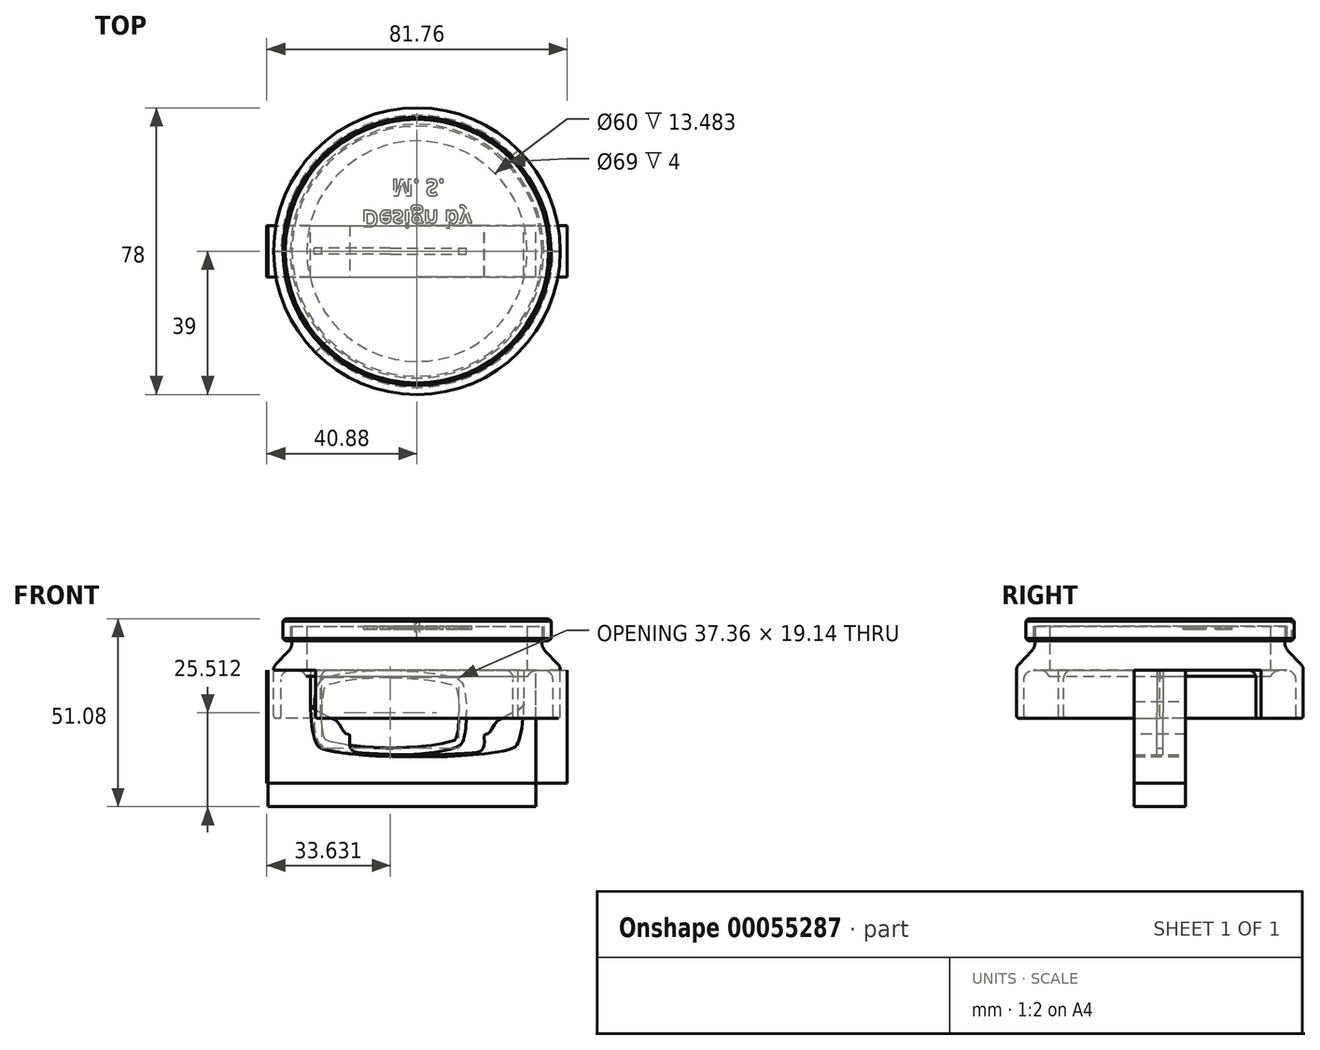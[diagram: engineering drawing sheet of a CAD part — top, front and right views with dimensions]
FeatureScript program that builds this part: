
annotation { "Feature Type Name" : "Feature", "Feature Type Description" : "" }
export const myFeature = defineFeature(function(context is Context, id is Id, definition is map)
    precondition{}
    {
        {
            var Q0;
            Q0=qCreatedBy(makeId("Top.planeOp"),FACE);
            cPlane(context, id + "F0", {"entities" : qUnion([Q0]), "cplaneType" : CPlaneType.OFFSET, "offset" : 14 * mm, "width" : 150 * mm, "height" : 150 * mm});
        }
        {
            var Q0;
            Q0=qCreatedBy(makeId("Front.planeOp"),FACE);
            var sketch = newSketch(context, id + "F1", { "sketchPlane" : qUnion([Q0])});
            skPoint(sketch, "E0.visualSharp", {"position": v(-30, 12) * mm});
            skLineSegment(sketch, "E1", {"start": v(-39, 0) * mm, "end": v(-39, 0.2) * mm});
            skLineSegment(sketch, "E2", {"start": v(-38.45, 1.58) * mm, "end": v(-36.66, 3.48) * mm});
            skPoint(sketch, "E3.visualSharp", {"position": v(-39, 1) * mm});
            skArc(sketch, "E3.filletArc", {"start": v(-38.45, 1.58) * mm, "mid": v(-38.86, 0.94) * mm, "end": v(-39, 0.2) * mm});
            skLineSegment(sketch, "E4", {"start": v(-30, 12) * mm, "end": v(-34, 12) * mm});
            skLineSegment(sketch, "E5", {"start": v(-34, 7.49) * mm, "end": v(-34, 12) * mm});
            skLineSegment(sketch, "E6", {"start": v(-36.66, 3.48) * mm, "end": v(-34.82, 5.43) * mm});
            skLineSegment(sketch, "E7", {"start": v(-34, 6.3) * mm, "end": v(-30, 6.3) * mm, "construction": true});
            skLineSegment(sketch, "E8", {"start": v(-30, 0) * mm, "end": v(-30, 6.3) * mm});
            skLineSegment(sketch, "E9", {"start": v(-30, 6.3) * mm, "end": v(-30, 12) * mm});
            skPoint(sketch, "E10.visualSharp", {"position": v(-34, 6.3) * mm});
            skArc(sketch, "E10.filletArc", {"start": v(-34.82, 5.43) * mm, "mid": v(-34.21, 6.38) * mm, "end": v(-34, 7.49) * mm});
            skLineSegment(sketch, "E11", {"start": v(-39, 0) * mm, "end": v(-32.6, 0) * mm});
            skLineSegment(sketch, "E12", {"start": v(-30, -2.6) * mm, "end": v(-30, -3) * mm});
            skPoint(sketch, "E13.visualSharp", {"position": v(-30, 0) * mm});
            skArc(sketch, "E13.filletArc", {"start": v(-30.23, -1.53) * mm, "mid": v(-31.19, -0.42) * mm, "end": v(-32.6, 0) * mm});
            skLineSegment(sketch, "E14", {"start": v(-30, 0) * mm, "end": v(-30, -1.48) * mm});
            skPoint(sketch, "E15.visualSharp", {"position": v(-30, -2.6) * mm});
            skArc(sketch, "E15.filletArc", {"start": v(-30.23, -1.53) * mm, "mid": v(-30.1, -1.6) * mm, "end": v(-30, -1.48) * mm});
            skSolve(sketch);
        }
        {
            var Q0;
            Q0=qCreatedBy(makeId("Front.planeOp"),FACE);
            var sketch = newSketch(context, id + "F2", { "sketchPlane" : qUnion([Q0])});
            skLineSegment(sketch, "E16", {"start": v(-37.6, -13) * mm, "end": v(-38.4, -13) * mm});
            skLineSegment(sketch, "E17", {"start": v(-39, -12.4) * mm, "end": v(-39, 0) * mm});
            skLineSegment(sketch, "E18", {"start": v(0, 17.79) * mm, "end": v(0, -24.2) * mm, "construction": true});
            skPoint(sketch, "E19.visualSharp", {"position": v(-39, -13) * mm});
            skArc(sketch, "E19.filletArc", {"start": v(-39, -12.4) * mm, "mid": v(-38.82, -12.82) * mm, "end": v(-38.4, -13) * mm});
            skPoint(sketch, "E20.visualSharp", {"position": v(-37, -13) * mm});
            skArc(sketch, "E20.filletArc", {"start": v(-37.6, -13) * mm, "mid": v(-37.18, -12.82) * mm, "end": v(-37, -12.4) * mm});
            skLineSegment(sketch, "E21", {"start": v(-37, -12.4) * mm, "end": v(-37, -2.5) * mm});
            skPoint(sketch, "E22.visualSharp", {"position": v(-37, 0) * mm});
            skArc(sketch, "E22.filletArc", {"start": v(-34.5, 0) * mm, "mid": v(-36.27, -0.73) * mm, "end": v(-37, -2.5) * mm});
            skLineSegment(sketch, "E23", {"start": v(-39, 0) * mm, "end": v(-34.5, 0) * mm});
            skLineSegment(sketch, "E24.MirrorCS", {"start": v(37, -12.4) * mm, "end": v(37, -2.5) * mm});
            skArc(sketch, "E25.MirrorCS", {"start": v(34.5, 0) * mm, "mid": v(36.27, -0.73) * mm, "end": v(37, -2.5) * mm});
            skLineSegment(sketch, "E26.MirrorCS", {"start": v(39, 0) * mm, "end": v(34.5, 0) * mm});
            skLineSegment(sketch, "E27.MirrorCS", {"start": v(39, -12.4) * mm, "end": v(39, 0) * mm});
            skArc(sketch, "E28.MirrorCS", {"start": v(39, -12.4) * mm, "mid": v(38.82, -12.82) * mm, "end": v(38.4, -13) * mm});
            skLineSegment(sketch, "E29.MirrorCS", {"start": v(37.6, -13) * mm, "end": v(38.4, -13) * mm});
            skArc(sketch, "E30.MirrorCS", {"start": v(37.6, -13) * mm, "mid": v(37.18, -12.82) * mm, "end": v(37, -12.4) * mm});
            skSolve(sketch);
        }
        {
            var Q0;
            Q0=qCreatedBy(makeId("Front.planeOp"),FACE);
            var sketch = newSketch(context, id + "F3", { "sketchPlane" : qUnion([Q0])});
            skLineSegment(sketch, "E31", {"start": v(0, 31.8) * mm, "end": v(0, -40.21) * mm});
            skSolve(sketch);
        }
        {
            var Q0;
            Q0=qCreatedBy(makeId("Front.planeOp"),FACE);
            var sketch = newSketch(context, id + "F4", { "sketchPlane" : qUnion([Q0])});
            skLineSegment(sketch, "E32", {"start": v(0, -41.34) * mm, "end": v(0, 43.33) * mm});
            skSolve(sketch);
        }
        {
            var Q0;
            Q0=qSketchRegion(id+"F1",true);
            var Q1;
            Q1=sQuery(id+"F4.wireOp",EDGE,"E32");
            revolve(context, id + "F5", {"entities" : qUnion([Q0]), "axis" : qUnion([Q1]), "revolveType" : RevolveType.FULL});
        }
        {
            var Q0;
            Q0=qSketchRegion(id+"F2",true);
            var Q1;
            Q1=sQuery(id+"F3.wireOp",EDGE,"E31");
            revolve(context, id + "F6", {"operationType" : NewBodyOperationType.ADD, "entities" : qUnion([Q0]), "axis" : qUnion([Q1]), "revolveType" : RevolveType.ONE_DIRECTION, "angle" : 135 * degree});
        }
        {
            var Q0;
            Q0=qCreatedBy(makeId("Front.planeOp"),FACE);
            var sketch = newSketch(context, id + "F7", { "sketchPlane" : qUnion([Q0])});
            skLineSegment(sketch, "E33", {"start": v(0, 0) * mm, "end": v(0, 12) * mm, "construction": true});
            skLineSegment(sketch, "E34", {"start": v(0, 12) * mm, "end": v(-34.5, 12) * mm});
            skLineSegment(sketch, "E35", {"start": v(-34.5, 12) * mm, "end": v(-34.5, 8) * mm});
            skLineSegment(sketch, "E36", {"start": v(0, 14) * mm, "end": v(0, 12) * mm});
            skLineSegment(sketch, "E37", {"start": v(-35.85, 14) * mm, "end": v(0, 14) * mm});
            skLineSegment(sketch, "E38", {"start": v(-35.85, 14) * mm, "end": v(-36.5, 14) * mm, "construction": true});
            skLineSegment(sketch, "E39", {"start": v(-36.5, 14) * mm, "end": v(-36.5, 13.35) * mm, "construction": true});
            skLineSegment(sketch, "E40", {"start": v(-34.5, 8) * mm, "end": v(-35.85, 8) * mm});
            skLineSegment(sketch, "E41", {"start": v(-35.85, 8) * mm, "end": v(-36.5, 8) * mm, "construction": true});
            skLineSegment(sketch, "E42", {"start": v(-36.5, 8) * mm, "end": v(-36.5, 8.65) * mm, "construction": true});
            skLineSegment(sketch, "E43", {"start": v(-36.5, 8.65) * mm, "end": v(-36.5, 13.35) * mm});
            skLineSegment(sketch, "E44", {"start": v(-36.5, 13.35) * mm, "end": v(-35.85, 14) * mm});
            skLineSegment(sketch, "E45", {"start": v(-36.5, 8.65) * mm, "end": v(-35.85, 8) * mm});
            skSolve(sketch);
        }
        {
            var Q0;
            Q0=qSketchRegion(id+"F7",true);
            var Q1;
            Q1=sQuery(id+"F7.wireOp",EDGE,"E33");
            revolve(context, id + "F8", {"entities" : qUnion([Q0]), "axis" : qUnion([Q1]), "revolveType" : RevolveType.FULL});
        }
        {
            var Q0;
            Q0=qCreatedBy(makeId("Front.planeOp"),FACE);
            var sketch = newSketch(context, id + "F9", { "sketchPlane" : qUnion([Q0])});
            skLineSegment(sketch, "E46", {"start": v(-29, 0) * mm, "end": v(-29, -9) * mm});
            skFitSpline(sketch, "E47", {"points": [v(-29, -9) * mm, v(-28.47, -16.14) * mm, v(-27.49, -19.68) * mm, v(-26.1, -21.19) * mm, v(-16.96, -22.83) * mm, v(0, -23.5) * mm], "startDerivative": vector(0, -32.22) * mm, "endDerivative": vector(91.72, 0) * mm});
            skLineSegment(sketch, "E48", {"start": v(-29, 0) * mm, "end": v(-40.88, 0) * mm});
            skLineSegment(sketch, "E49", {"start": v(-40.88, 0) * mm, "end": v(-40.88, -30.69) * mm});
            skLineSegment(sketch, "E50", {"start": v(-40.88, -30.69) * mm, "end": v(0, -30.69) * mm});
            skLineSegment(sketch, "E51", {"start": v(0, -23.5) * mm, "end": v(0, -30.69) * mm, "construction": true});
            skFitSpline(sketch, "E52.MirrorCS", {"points": [v(29, -9) * mm, v(28.47, -16.14) * mm, v(27.49, -19.68) * mm, v(26.1, -21.19) * mm, v(16.96, -22.83) * mm, v(0, -23.5) * mm], "startDerivative": vector(0, -32.22) * mm, "endDerivative": vector(-91.72, 0) * mm});
            skLineSegment(sketch, "E53.MirrorCS", {"start": v(29, 0) * mm, "end": v(29, -9) * mm});
            skLineSegment(sketch, "E54.MirrorCS", {"start": v(29, 0) * mm, "end": v(40.88, 0) * mm});
            skLineSegment(sketch, "E55.MirrorCS", {"start": v(40.88, 0) * mm, "end": v(40.88, -30.69) * mm});
            skLineSegment(sketch, "E56.MirrorCS", {"start": v(40.88, -30.69) * mm, "end": v(0, -30.69) * mm});
            skLineSegment(sketch, "E57", {"start": v(0, -23.5) * mm, "end": v(0, 0) * mm, "construction": true});
            skLineSegment(sketch, "E58", {"start": v(0, 0) * mm, "end": v(-29, 0) * mm, "construction": true});
            skLineSegment(sketch, "E59.MirrorCS", {"start": v(0, 0) * mm, "end": v(29, 0) * mm, "construction": true});
            skSolve(sketch);
        }
        {
            var Q0;
            Q0=qCreatedBy(makeId("Front.planeOp"),FACE);
            var sketch = newSketch(context, id + "F10", { "sketchPlane" : qUnion([Q0])});
            skLineSegment(sketch, "E60", {"start": v(-29, 0) * mm, "end": v(-29, -8.5) * mm});
            skFitSpline(sketch, "E61", {"points": [v(-29, -8.5) * mm, v(-28.88, -9.5) * mm, v(-28.02, -10.51) * mm, v(-26.18, -11.49) * mm, v(-23.57, -12.82) * mm, v(-21.3, -14.4) * mm, v(-19.3, -17.26) * mm, v(-18.46, -17.42) * mm, v(-18.34, -20) * mm, v(-17.7, -21.61) * mm, v(-15, -22.45) * mm, v(0, -23) * mm], "startDerivative": vector(0.66, -15.21) * mm, "endDerivative": vector(12.35, 0) * mm});
            skLineSegment(sketch, "E62.MirrorCS", {"start": v(29, 0) * mm, "end": v(29, -8.5) * mm});
            skFitSpline(sketch, "E63.MirrorCS", {"points": [v(29, -8.5) * mm, v(28.88, -9.5) * mm, v(28.02, -10.51) * mm, v(26.18, -11.49) * mm, v(23.57, -12.82) * mm, v(21.3, -14.4) * mm, v(19.3, -17.26) * mm, v(18.46, -17.42) * mm, v(18.34, -20) * mm, v(17.7, -21.61) * mm, v(15, -22.45) * mm, v(0, -23) * mm], "startDerivative": vector(-0.66, -15.21) * mm, "endDerivative": vector(-12.35, 0) * mm});
            skLineSegment(sketch, "E64", {"start": v(-29, 0) * mm, "end": v(-40.5, 0) * mm});
            skLineSegment(sketch, "E65", {"start": v(-40.5, 0) * mm, "end": v(-40.5, -37.08) * mm});
            skLineSegment(sketch, "E66", {"start": v(-40.5, -37.08) * mm, "end": v(32.41, -37.08) * mm});
            skLineSegment(sketch, "E67", {"start": v(32.41, -37.08) * mm, "end": v(32.41, 0) * mm});
            skLineSegment(sketch, "E68", {"start": v(32.41, 0) * mm, "end": v(29, 0) * mm});
            skSolve(sketch);
        }
        {
            var Q0;
            Q0=qSketchRegion(id+"F10",true);
            extrude(context, id + "F11", {"entities" : qUnion([Q0]), "endBound" : BoundingType.SYMMETRIC, "depth" : 14 * mm});
        }
        {
            var Q0;
            Q0=makeQuery(id+"F9.imprint","IMPRINT",FACE,{"disambiguationData":[TD([[makeQuery(id+"F9.imprint","IMPRINT",EDGE,{"derivedFrom":sQuery(id+"F9.wireOp",EDGE,"E46")}),-1.0]])]});
            var Q1;
            Q1=makeQuery(id+"F9.imprint","IMPRINT",FACE,{"disambiguationData":[TD([[makeQuery(id+"F9.imprint","IMPRINT",EDGE,{"derivedFrom":sQuery(id+"F9.wireOp",EDGE,"E51")}),1.0]])]});
            extrude(context, id + "F12", {"entities" : qUnion([Q0, Q1]), "endBound" : BoundingType.SYMMETRIC, "depth" : 14 * mm});
        }
        {
            var Q0;
            Q0=makeQuery(id+"F8.opRevolve","SWEPT_FACE",FACE,{"disambiguationData":[OSD([sQuery(id+"F7.wireOp",EDGE,"E34")])]});
            var sketch = newSketch(context, id + "F13", { "sketchPlane" : qUnion([Q0])});
            skText(sketch, "E69", { "text": "Design by\n     M. S.", "fontName": "OpenSans-Bold.ttf"});
            const initialGuessF13  = {"E69": [-0.015, -0.01107, 1, 0, 0.00448]};
            skSetInitialGuess(sketch, initialGuessF13);
            skSolve(sketch);
        }
        {
            var Q0;
            Q0=qSketchRegion(id+"F13",true);
            extrude(context, id + "F14", {"entities" : qUnion([Q0]), "operationType" : NewBodyOperationType.ADD, "depth" : 0.8 * mm});
        }
        {
            var Q0;
            Q0=qCreatedBy(id+"F0.planeOp",FACE);
            var sketch = newSketch(context, id + "F15", { "sketchPlane" : qUnion([Q0])});
            skLineSegment(sketch, "E70", {"start": v(0, 36.5) * mm, "end": v(-0.65, 36.5) * mm});
            skLineSegment(sketch, "E71", {"start": v(-0.65, 36.5) * mm, "end": v(0, 35.85) * mm});
            skLineSegment(sketch, "E72", {"start": v(0, 35.85) * mm, "end": v(0, 36.5) * mm, "construction": true});
            skLineSegment(sketch, "E73.MirrorCS", {"start": v(0.65, 36.5) * mm, "end": v(0, 35.85) * mm});
            skLineSegment(sketch, "E74.MirrorCS", {"start": v(0, 36.5) * mm, "end": v(0.65, 36.5) * mm});
            skSolve(sketch);
        }
        {
            var Q0;
            {var subQ0=sQuery(id+"F15.wireOp",EDGE,"E73.MirrorCS");var subQ1=sQuery(id+"F15.wireOp",EDGE,"E71");var subQ2=makeQuery(id+"F15.imprint","INTERSECT",VERTEX,{"derivedFrom":[subQ1,subQ0]});Q0=makeQuery(id+"F15.imprint","IMPRINT",FACE,{"disambiguationData":[TD([[makeQuery(id+"F15.imprint","IMPRINT",EDGE,{"disambiguationData":[TD([[subQ2,1.0]])],"derivedFrom":subQ1}),1.0]])]});}
            var Q1;
            Q1=makeQuery(id+"F8.opRevolve","SWEPT_FACE",FACE,{"disambiguationData":[OSD([sQuery(id+"F7.wireOp",EDGE,"E40")])]});
            extrude(context, id + "F16", {"entities" : qUnion([Q0]), "endBound" : BoundingType.UP_TO_SURFACE, "oppositeDirection" : true, "endBoundEntityFace" : qUnion([Q1]), "depth" : 5 * mm});
        }
        {
            var Q0;
            Q0=makeQuery(id+"F16.opExtrude","SWEPT_BODY",BODY,{"disambiguationData":[OSD([sQuery(id+"F15.wireOp",EDGE,"E70"),sQuery(id+"F15.wireOp",EDGE,"E71"),sQuery(id+"F15.wireOp",EDGE,"E73.MirrorCS"),sQuery(id+"F15.wireOp",EDGE,"E74.MirrorCS")])]});
            var Q1;
            Q1=makeQuery(id+"FeenwNvDrwZ4BJb_3.1.F16.opExtrude","SWEPT_BODY",BODY,{"disambiguationData":[OSD([sQuery(id+"F15.wireOp",EDGE,"E70"),sQuery(id+"F15.wireOp",EDGE,"E71"),sQuery(id+"F15.wireOp",EDGE,"E73.MirrorCS"),sQuery(id+"F15.wireOp",EDGE,"E74.MirrorCS")])]});
            var Q2;
            Q2=makeQuery(id+"FeenwNvDrwZ4BJb_3.2.F16.opExtrude","SWEPT_BODY",BODY,{"disambiguationData":[OSD([sQuery(id+"F15.wireOp",EDGE,"E70"),sQuery(id+"F15.wireOp",EDGE,"E71"),sQuery(id+"F15.wireOp",EDGE,"E73.MirrorCS"),sQuery(id+"F15.wireOp",EDGE,"E74.MirrorCS")])]});
            var Q3;
            Q3=makeQuery(id+"FeenwNvDrwZ4BJb_3.3.F16.opExtrude","SWEPT_BODY",BODY,{"disambiguationData":[OSD([sQuery(id+"F15.wireOp",EDGE,"E70"),sQuery(id+"F15.wireOp",EDGE,"E71"),sQuery(id+"F15.wireOp",EDGE,"E73.MirrorCS"),sQuery(id+"F15.wireOp",EDGE,"E74.MirrorCS")])]});
            var Q4;
            Q4=makeQuery(id+"FeenwNvDrwZ4BJb_3.4.F16.opExtrude","SWEPT_BODY",BODY,{"disambiguationData":[OSD([sQuery(id+"F15.wireOp",EDGE,"E70"),sQuery(id+"F15.wireOp",EDGE,"E71"),sQuery(id+"F15.wireOp",EDGE,"E73.MirrorCS"),sQuery(id+"F15.wireOp",EDGE,"E74.MirrorCS")])]});
            var Q5;
            Q5=makeQuery(id+"FeenwNvDrwZ4BJb_3.5.F16.opExtrude","SWEPT_BODY",BODY,{"disambiguationData":[OSD([sQuery(id+"F15.wireOp",EDGE,"E70"),sQuery(id+"F15.wireOp",EDGE,"E71"),sQuery(id+"F15.wireOp",EDGE,"E73.MirrorCS"),sQuery(id+"F15.wireOp",EDGE,"E74.MirrorCS")])]});
            var Q6;
            Q6=makeQuery(id+"FeenwNvDrwZ4BJb_3.6.F16.opExtrude","SWEPT_BODY",BODY,{"disambiguationData":[OSD([sQuery(id+"F15.wireOp",EDGE,"E70"),sQuery(id+"F15.wireOp",EDGE,"E71"),sQuery(id+"F15.wireOp",EDGE,"E73.MirrorCS"),sQuery(id+"F15.wireOp",EDGE,"E74.MirrorCS")])]});
            var Q7;
            Q7=makeQuery(id+"FeenwNvDrwZ4BJb_3.7.F16.opExtrude","SWEPT_BODY",BODY,{"disambiguationData":[OSD([sQuery(id+"F15.wireOp",EDGE,"E70"),sQuery(id+"F15.wireOp",EDGE,"E71"),sQuery(id+"F15.wireOp",EDGE,"E73.MirrorCS"),sQuery(id+"F15.wireOp",EDGE,"E74.MirrorCS")])]});
            var Q8;
            Q8=makeQuery(id+"FeenwNvDrwZ4BJb_3.8.F16.opExtrude","SWEPT_BODY",BODY,{"disambiguationData":[OSD([sQuery(id+"F15.wireOp",EDGE,"E70"),sQuery(id+"F15.wireOp",EDGE,"E71"),sQuery(id+"F15.wireOp",EDGE,"E73.MirrorCS"),sQuery(id+"F15.wireOp",EDGE,"E74.MirrorCS")])]});
            var Q9;
            Q9=makeQuery(id+"FeenwNvDrwZ4BJb_3.9.F16.opExtrude","SWEPT_BODY",BODY,{"disambiguationData":[OSD([sQuery(id+"F15.wireOp",EDGE,"E70"),sQuery(id+"F15.wireOp",EDGE,"E71"),sQuery(id+"F15.wireOp",EDGE,"E73.MirrorCS"),sQuery(id+"F15.wireOp",EDGE,"E74.MirrorCS")])]});
            var Q10;
            Q10=makeQuery(id+"FeenwNvDrwZ4BJb_3.10.F16.opExtrude","SWEPT_BODY",BODY,{"disambiguationData":[OSD([sQuery(id+"F15.wireOp",EDGE,"E70"),sQuery(id+"F15.wireOp",EDGE,"E71"),sQuery(id+"F15.wireOp",EDGE,"E73.MirrorCS"),sQuery(id+"F15.wireOp",EDGE,"E74.MirrorCS")])]});
            var Q11;
            Q11=makeQuery(id+"FeenwNvDrwZ4BJb_3.11.F16.opExtrude","SWEPT_BODY",BODY,{"disambiguationData":[OSD([sQuery(id+"F15.wireOp",EDGE,"E70"),sQuery(id+"F15.wireOp",EDGE,"E71"),sQuery(id+"F15.wireOp",EDGE,"E73.MirrorCS"),sQuery(id+"F15.wireOp",EDGE,"E74.MirrorCS")])]});
            var Q12;
            Q12=makeQuery(id+"FeenwNvDrwZ4BJb_3.12.F16.opExtrude","SWEPT_BODY",BODY,{"disambiguationData":[OSD([sQuery(id+"F15.wireOp",EDGE,"E70"),sQuery(id+"F15.wireOp",EDGE,"E71"),sQuery(id+"F15.wireOp",EDGE,"E73.MirrorCS"),sQuery(id+"F15.wireOp",EDGE,"E74.MirrorCS")])]});
            var Q13;
            Q13=makeQuery(id+"FeenwNvDrwZ4BJb_3.13.F16.opExtrude","SWEPT_BODY",BODY,{"disambiguationData":[OSD([sQuery(id+"F15.wireOp",EDGE,"E70"),sQuery(id+"F15.wireOp",EDGE,"E71"),sQuery(id+"F15.wireOp",EDGE,"E73.MirrorCS"),sQuery(id+"F15.wireOp",EDGE,"E74.MirrorCS")])]});
            var Q14;
            Q14=makeQuery(id+"FeenwNvDrwZ4BJb_3.14.F16.opExtrude","SWEPT_BODY",BODY,{"disambiguationData":[OSD([sQuery(id+"F15.wireOp",EDGE,"E70"),sQuery(id+"F15.wireOp",EDGE,"E71"),sQuery(id+"F15.wireOp",EDGE,"E73.MirrorCS"),sQuery(id+"F15.wireOp",EDGE,"E74.MirrorCS")])]});
            var Q15;
            Q15=makeQuery(id+"FeenwNvDrwZ4BJb_3.15.F16.opExtrude","SWEPT_BODY",BODY,{"disambiguationData":[OSD([sQuery(id+"F15.wireOp",EDGE,"E70"),sQuery(id+"F15.wireOp",EDGE,"E71"),sQuery(id+"F15.wireOp",EDGE,"E73.MirrorCS"),sQuery(id+"F15.wireOp",EDGE,"E74.MirrorCS")])]});
            var Q16;
            Q16=makeQuery(id+"FeenwNvDrwZ4BJb_3.16.F16.opExtrude","SWEPT_BODY",BODY,{"disambiguationData":[OSD([sQuery(id+"F15.wireOp",EDGE,"E70"),sQuery(id+"F15.wireOp",EDGE,"E71"),sQuery(id+"F15.wireOp",EDGE,"E73.MirrorCS"),sQuery(id+"F15.wireOp",EDGE,"E74.MirrorCS")])]});
            var Q17;
            Q17=makeQuery(id+"FeenwNvDrwZ4BJb_3.17.F16.opExtrude","SWEPT_BODY",BODY,{"disambiguationData":[OSD([sQuery(id+"F15.wireOp",EDGE,"E70"),sQuery(id+"F15.wireOp",EDGE,"E71"),sQuery(id+"F15.wireOp",EDGE,"E73.MirrorCS"),sQuery(id+"F15.wireOp",EDGE,"E74.MirrorCS")])]});
            var Q18;
            Q18=makeQuery(id+"FeenwNvDrwZ4BJb_3.18.F16.opExtrude","SWEPT_BODY",BODY,{"disambiguationData":[OSD([sQuery(id+"F15.wireOp",EDGE,"E70"),sQuery(id+"F15.wireOp",EDGE,"E71"),sQuery(id+"F15.wireOp",EDGE,"E73.MirrorCS"),sQuery(id+"F15.wireOp",EDGE,"E74.MirrorCS")])]});
            var Q19;
            Q19=makeQuery(id+"FeenwNvDrwZ4BJb_3.19.F16.opExtrude","SWEPT_BODY",BODY,{"disambiguationData":[OSD([sQuery(id+"F15.wireOp",EDGE,"E70"),sQuery(id+"F15.wireOp",EDGE,"E71"),sQuery(id+"F15.wireOp",EDGE,"E73.MirrorCS"),sQuery(id+"F15.wireOp",EDGE,"E74.MirrorCS")])]});
            var Q20;
            Q20=makeQuery(id+"FeenwNvDrwZ4BJb_3.20.F16.opExtrude","SWEPT_BODY",BODY,{"disambiguationData":[OSD([sQuery(id+"F15.wireOp",EDGE,"E70"),sQuery(id+"F15.wireOp",EDGE,"E71"),sQuery(id+"F15.wireOp",EDGE,"E73.MirrorCS"),sQuery(id+"F15.wireOp",EDGE,"E74.MirrorCS")])]});
            var Q21;
            Q21=makeQuery(id+"FeenwNvDrwZ4BJb_3.21.F16.opExtrude","SWEPT_BODY",BODY,{"disambiguationData":[OSD([sQuery(id+"F15.wireOp",EDGE,"E70"),sQuery(id+"F15.wireOp",EDGE,"E71"),sQuery(id+"F15.wireOp",EDGE,"E73.MirrorCS"),sQuery(id+"F15.wireOp",EDGE,"E74.MirrorCS")])]});
            var Q22;
            Q22=makeQuery(id+"FeenwNvDrwZ4BJb_3.22.F16.opExtrude","SWEPT_BODY",BODY,{"disambiguationData":[OSD([sQuery(id+"F15.wireOp",EDGE,"E70"),sQuery(id+"F15.wireOp",EDGE,"E71"),sQuery(id+"F15.wireOp",EDGE,"E73.MirrorCS"),sQuery(id+"F15.wireOp",EDGE,"E74.MirrorCS")])]});
            var Q23;
            Q23=makeQuery(id+"FeenwNvDrwZ4BJb_3.23.F16.opExtrude","SWEPT_BODY",BODY,{"disambiguationData":[OSD([sQuery(id+"F15.wireOp",EDGE,"E70"),sQuery(id+"F15.wireOp",EDGE,"E71"),sQuery(id+"F15.wireOp",EDGE,"E73.MirrorCS"),sQuery(id+"F15.wireOp",EDGE,"E74.MirrorCS")])]});
            var Q24;
            Q24=makeQuery(id+"FeenwNvDrwZ4BJb_3.24.F16.opExtrude","SWEPT_BODY",BODY,{"disambiguationData":[OSD([sQuery(id+"F15.wireOp",EDGE,"E70"),sQuery(id+"F15.wireOp",EDGE,"E71"),sQuery(id+"F15.wireOp",EDGE,"E73.MirrorCS"),sQuery(id+"F15.wireOp",EDGE,"E74.MirrorCS")])]});
            var Q25;
            Q25=makeQuery(id+"FeenwNvDrwZ4BJb_3.25.F16.opExtrude","SWEPT_BODY",BODY,{"disambiguationData":[OSD([sQuery(id+"F15.wireOp",EDGE,"E70"),sQuery(id+"F15.wireOp",EDGE,"E71"),sQuery(id+"F15.wireOp",EDGE,"E73.MirrorCS"),sQuery(id+"F15.wireOp",EDGE,"E74.MirrorCS")])]});
            var Q26;
            Q26=makeQuery(id+"FeenwNvDrwZ4BJb_3.26.F16.opExtrude","SWEPT_BODY",BODY,{"disambiguationData":[OSD([sQuery(id+"F15.wireOp",EDGE,"E70"),sQuery(id+"F15.wireOp",EDGE,"E71"),sQuery(id+"F15.wireOp",EDGE,"E73.MirrorCS"),sQuery(id+"F15.wireOp",EDGE,"E74.MirrorCS")])]});
            var Q27;
            Q27=makeQuery(id+"FeenwNvDrwZ4BJb_3.27.F16.opExtrude","SWEPT_BODY",BODY,{"disambiguationData":[OSD([sQuery(id+"F15.wireOp",EDGE,"E70"),sQuery(id+"F15.wireOp",EDGE,"E71"),sQuery(id+"F15.wireOp",EDGE,"E73.MirrorCS"),sQuery(id+"F15.wireOp",EDGE,"E74.MirrorCS")])]});
            var Q28;
            Q28=makeQuery(id+"FeenwNvDrwZ4BJb_3.28.F16.opExtrude","SWEPT_BODY",BODY,{"disambiguationData":[OSD([sQuery(id+"F15.wireOp",EDGE,"E70"),sQuery(id+"F15.wireOp",EDGE,"E71"),sQuery(id+"F15.wireOp",EDGE,"E73.MirrorCS"),sQuery(id+"F15.wireOp",EDGE,"E74.MirrorCS")])]});
            var Q29;
            Q29=makeQuery(id+"FeenwNvDrwZ4BJb_3.29.F16.opExtrude","SWEPT_BODY",BODY,{"disambiguationData":[OSD([sQuery(id+"F15.wireOp",EDGE,"E70"),sQuery(id+"F15.wireOp",EDGE,"E71"),sQuery(id+"F15.wireOp",EDGE,"E73.MirrorCS"),sQuery(id+"F15.wireOp",EDGE,"E74.MirrorCS")])]});
            var Q30;
            Q30=makeQuery(id+"FeenwNvDrwZ4BJb_3.30.F16.opExtrude","SWEPT_BODY",BODY,{"disambiguationData":[OSD([sQuery(id+"F15.wireOp",EDGE,"E70"),sQuery(id+"F15.wireOp",EDGE,"E71"),sQuery(id+"F15.wireOp",EDGE,"E73.MirrorCS"),sQuery(id+"F15.wireOp",EDGE,"E74.MirrorCS")])]});
            var Q31;
            Q31=makeQuery(id+"FeenwNvDrwZ4BJb_3.31.F16.opExtrude","SWEPT_BODY",BODY,{"disambiguationData":[OSD([sQuery(id+"F15.wireOp",EDGE,"E70"),sQuery(id+"F15.wireOp",EDGE,"E71"),sQuery(id+"F15.wireOp",EDGE,"E73.MirrorCS"),sQuery(id+"F15.wireOp",EDGE,"E74.MirrorCS")])]});
            var Q32;
            Q32=makeQuery(id+"FeenwNvDrwZ4BJb_3.32.F16.opExtrude","SWEPT_BODY",BODY,{"disambiguationData":[OSD([sQuery(id+"F15.wireOp",EDGE,"E70"),sQuery(id+"F15.wireOp",EDGE,"E71"),sQuery(id+"F15.wireOp",EDGE,"E73.MirrorCS"),sQuery(id+"F15.wireOp",EDGE,"E74.MirrorCS")])]});
            var Q33;
            Q33=makeQuery(id+"FeenwNvDrwZ4BJb_3.33.F16.opExtrude","SWEPT_BODY",BODY,{"disambiguationData":[OSD([sQuery(id+"F15.wireOp",EDGE,"E70"),sQuery(id+"F15.wireOp",EDGE,"E71"),sQuery(id+"F15.wireOp",EDGE,"E73.MirrorCS"),sQuery(id+"F15.wireOp",EDGE,"E74.MirrorCS")])]});
            var Q34;
            Q34=makeQuery(id+"FeenwNvDrwZ4BJb_3.34.F16.opExtrude","SWEPT_BODY",BODY,{"disambiguationData":[OSD([sQuery(id+"F15.wireOp",EDGE,"E70"),sQuery(id+"F15.wireOp",EDGE,"E71"),sQuery(id+"F15.wireOp",EDGE,"E73.MirrorCS"),sQuery(id+"F15.wireOp",EDGE,"E74.MirrorCS")])]});
            var Q35;
            Q35=makeQuery(id+"FeenwNvDrwZ4BJb_3.35.F16.opExtrude","SWEPT_BODY",BODY,{"disambiguationData":[OSD([sQuery(id+"F15.wireOp",EDGE,"E70"),sQuery(id+"F15.wireOp",EDGE,"E71"),sQuery(id+"F15.wireOp",EDGE,"E73.MirrorCS"),sQuery(id+"F15.wireOp",EDGE,"E74.MirrorCS")])]});
            var Q36;
            Q36=makeQuery(id+"FeenwNvDrwZ4BJb_3.36.F16.opExtrude","SWEPT_BODY",BODY,{"disambiguationData":[OSD([sQuery(id+"F15.wireOp",EDGE,"E70"),sQuery(id+"F15.wireOp",EDGE,"E71"),sQuery(id+"F15.wireOp",EDGE,"E73.MirrorCS"),sQuery(id+"F15.wireOp",EDGE,"E74.MirrorCS")])]});
            var Q37;
            Q37=makeQuery(id+"FeenwNvDrwZ4BJb_3.37.F16.opExtrude","SWEPT_BODY",BODY,{"disambiguationData":[OSD([sQuery(id+"F15.wireOp",EDGE,"E70"),sQuery(id+"F15.wireOp",EDGE,"E71"),sQuery(id+"F15.wireOp",EDGE,"E73.MirrorCS"),sQuery(id+"F15.wireOp",EDGE,"E74.MirrorCS")])]});
            var Q38;
            Q38=makeQuery(id+"FeenwNvDrwZ4BJb_3.38.F16.opExtrude","SWEPT_BODY",BODY,{"disambiguationData":[OSD([sQuery(id+"F15.wireOp",EDGE,"E70"),sQuery(id+"F15.wireOp",EDGE,"E71"),sQuery(id+"F15.wireOp",EDGE,"E73.MirrorCS"),sQuery(id+"F15.wireOp",EDGE,"E74.MirrorCS")])]});
            var Q39;
            Q39=makeQuery(id+"FeenwNvDrwZ4BJb_3.39.F16.opExtrude","SWEPT_BODY",BODY,{"disambiguationData":[OSD([sQuery(id+"F15.wireOp",EDGE,"E70"),sQuery(id+"F15.wireOp",EDGE,"E71"),sQuery(id+"F15.wireOp",EDGE,"E73.MirrorCS"),sQuery(id+"F15.wireOp",EDGE,"E74.MirrorCS")])]});
            var Q40;
            Q40=makeQuery(id+"FeenwNvDrwZ4BJb_3.40.F16.opExtrude","SWEPT_BODY",BODY,{"disambiguationData":[OSD([sQuery(id+"F15.wireOp",EDGE,"E70"),sQuery(id+"F15.wireOp",EDGE,"E71"),sQuery(id+"F15.wireOp",EDGE,"E73.MirrorCS"),sQuery(id+"F15.wireOp",EDGE,"E74.MirrorCS")])]});
            var Q41;
            Q41=makeQuery(id+"FeenwNvDrwZ4BJb_3.41.F16.opExtrude","SWEPT_BODY",BODY,{"disambiguationData":[OSD([sQuery(id+"F15.wireOp",EDGE,"E70"),sQuery(id+"F15.wireOp",EDGE,"E71"),sQuery(id+"F15.wireOp",EDGE,"E73.MirrorCS"),sQuery(id+"F15.wireOp",EDGE,"E74.MirrorCS")])]});
            var Q42;
            Q42=makeQuery(id+"FeenwNvDrwZ4BJb_3.42.F16.opExtrude","SWEPT_BODY",BODY,{"disambiguationData":[OSD([sQuery(id+"F15.wireOp",EDGE,"E70"),sQuery(id+"F15.wireOp",EDGE,"E71"),sQuery(id+"F15.wireOp",EDGE,"E73.MirrorCS"),sQuery(id+"F15.wireOp",EDGE,"E74.MirrorCS")])]});
            var Q43;
            Q43=makeQuery(id+"FeenwNvDrwZ4BJb_3.43.F16.opExtrude","SWEPT_BODY",BODY,{"disambiguationData":[OSD([sQuery(id+"F15.wireOp",EDGE,"E70"),sQuery(id+"F15.wireOp",EDGE,"E71"),sQuery(id+"F15.wireOp",EDGE,"E73.MirrorCS"),sQuery(id+"F15.wireOp",EDGE,"E74.MirrorCS")])]});
            var Q44;
            Q44=makeQuery(id+"FeenwNvDrwZ4BJb_3.44.F16.opExtrude","SWEPT_BODY",BODY,{"disambiguationData":[OSD([sQuery(id+"F15.wireOp",EDGE,"E70"),sQuery(id+"F15.wireOp",EDGE,"E71"),sQuery(id+"F15.wireOp",EDGE,"E73.MirrorCS"),sQuery(id+"F15.wireOp",EDGE,"E74.MirrorCS")])]});
            var Q45;
            Q45=makeQuery(id+"FeenwNvDrwZ4BJb_3.45.F16.opExtrude","SWEPT_BODY",BODY,{"disambiguationData":[OSD([sQuery(id+"F15.wireOp",EDGE,"E70"),sQuery(id+"F15.wireOp",EDGE,"E71"),sQuery(id+"F15.wireOp",EDGE,"E73.MirrorCS"),sQuery(id+"F15.wireOp",EDGE,"E74.MirrorCS")])]});
            var Q46;
            Q46=makeQuery(id+"FeenwNvDrwZ4BJb_3.46.F16.opExtrude","SWEPT_BODY",BODY,{"disambiguationData":[OSD([sQuery(id+"F15.wireOp",EDGE,"E70"),sQuery(id+"F15.wireOp",EDGE,"E71"),sQuery(id+"F15.wireOp",EDGE,"E73.MirrorCS"),sQuery(id+"F15.wireOp",EDGE,"E74.MirrorCS")])]});
            var Q47;
            Q47=makeQuery(id+"FeenwNvDrwZ4BJb_3.47.F16.opExtrude","SWEPT_BODY",BODY,{"disambiguationData":[OSD([sQuery(id+"F15.wireOp",EDGE,"E70"),sQuery(id+"F15.wireOp",EDGE,"E71"),sQuery(id+"F15.wireOp",EDGE,"E73.MirrorCS"),sQuery(id+"F15.wireOp",EDGE,"E74.MirrorCS")])]});
            var Q48;
            Q48=makeQuery(id+"FeenwNvDrwZ4BJb_3.48.F16.opExtrude","SWEPT_BODY",BODY,{"disambiguationData":[OSD([sQuery(id+"F15.wireOp",EDGE,"E70"),sQuery(id+"F15.wireOp",EDGE,"E71"),sQuery(id+"F15.wireOp",EDGE,"E73.MirrorCS"),sQuery(id+"F15.wireOp",EDGE,"E74.MirrorCS")])]});
            var Q49;
            Q49=makeQuery(id+"FeenwNvDrwZ4BJb_3.49.F16.opExtrude","SWEPT_BODY",BODY,{"disambiguationData":[OSD([sQuery(id+"F15.wireOp",EDGE,"E70"),sQuery(id+"F15.wireOp",EDGE,"E71"),sQuery(id+"F15.wireOp",EDGE,"E73.MirrorCS"),sQuery(id+"F15.wireOp",EDGE,"E74.MirrorCS")])]});
            var Q50;
            Q50=makeQuery(id+"FeenwNvDrwZ4BJb_3.50.F16.opExtrude","SWEPT_BODY",BODY,{"disambiguationData":[OSD([sQuery(id+"F15.wireOp",EDGE,"E70"),sQuery(id+"F15.wireOp",EDGE,"E71"),sQuery(id+"F15.wireOp",EDGE,"E73.MirrorCS"),sQuery(id+"F15.wireOp",EDGE,"E74.MirrorCS")])]});
            var Q51;
            Q51=makeQuery(id+"FeenwNvDrwZ4BJb_3.51.F16.opExtrude","SWEPT_BODY",BODY,{"disambiguationData":[OSD([sQuery(id+"F15.wireOp",EDGE,"E70"),sQuery(id+"F15.wireOp",EDGE,"E71"),sQuery(id+"F15.wireOp",EDGE,"E73.MirrorCS"),sQuery(id+"F15.wireOp",EDGE,"E74.MirrorCS")])]});
            var Q52;
            Q52=makeQuery(id+"FeenwNvDrwZ4BJb_3.52.F16.opExtrude","SWEPT_BODY",BODY,{"disambiguationData":[OSD([sQuery(id+"F15.wireOp",EDGE,"E70"),sQuery(id+"F15.wireOp",EDGE,"E71"),sQuery(id+"F15.wireOp",EDGE,"E73.MirrorCS"),sQuery(id+"F15.wireOp",EDGE,"E74.MirrorCS")])]});
            var Q53;
            Q53=makeQuery(id+"FeenwNvDrwZ4BJb_3.53.F16.opExtrude","SWEPT_BODY",BODY,{"disambiguationData":[OSD([sQuery(id+"F15.wireOp",EDGE,"E70"),sQuery(id+"F15.wireOp",EDGE,"E71"),sQuery(id+"F15.wireOp",EDGE,"E73.MirrorCS"),sQuery(id+"F15.wireOp",EDGE,"E74.MirrorCS")])]});
            var Q54;
            Q54=makeQuery(id+"FeenwNvDrwZ4BJb_3.54.F16.opExtrude","SWEPT_BODY",BODY,{"disambiguationData":[OSD([sQuery(id+"F15.wireOp",EDGE,"E70"),sQuery(id+"F15.wireOp",EDGE,"E71"),sQuery(id+"F15.wireOp",EDGE,"E73.MirrorCS"),sQuery(id+"F15.wireOp",EDGE,"E74.MirrorCS")])]});
            var Q55;
            Q55=makeQuery(id+"FeenwNvDrwZ4BJb_3.55.F16.opExtrude","SWEPT_BODY",BODY,{"disambiguationData":[OSD([sQuery(id+"F15.wireOp",EDGE,"E70"),sQuery(id+"F15.wireOp",EDGE,"E71"),sQuery(id+"F15.wireOp",EDGE,"E73.MirrorCS"),sQuery(id+"F15.wireOp",EDGE,"E74.MirrorCS")])]});
            var Q56;
            Q56=makeQuery(id+"FeenwNvDrwZ4BJb_3.56.F16.opExtrude","SWEPT_BODY",BODY,{"disambiguationData":[OSD([sQuery(id+"F15.wireOp",EDGE,"E70"),sQuery(id+"F15.wireOp",EDGE,"E71"),sQuery(id+"F15.wireOp",EDGE,"E73.MirrorCS"),sQuery(id+"F15.wireOp",EDGE,"E74.MirrorCS")])]});
            var Q57;
            Q57=makeQuery(id+"FeenwNvDrwZ4BJb_3.57.F16.opExtrude","SWEPT_BODY",BODY,{"disambiguationData":[OSD([sQuery(id+"F15.wireOp",EDGE,"E70"),sQuery(id+"F15.wireOp",EDGE,"E71"),sQuery(id+"F15.wireOp",EDGE,"E73.MirrorCS"),sQuery(id+"F15.wireOp",EDGE,"E74.MirrorCS")])]});
            var Q58;
            Q58=makeQuery(id+"FeenwNvDrwZ4BJb_3.58.F16.opExtrude","SWEPT_BODY",BODY,{"disambiguationData":[OSD([sQuery(id+"F15.wireOp",EDGE,"E70"),sQuery(id+"F15.wireOp",EDGE,"E71"),sQuery(id+"F15.wireOp",EDGE,"E73.MirrorCS"),sQuery(id+"F15.wireOp",EDGE,"E74.MirrorCS")])]});
            var Q59;
            Q59=makeQuery(id+"FeenwNvDrwZ4BJb_3.59.F16.opExtrude","SWEPT_BODY",BODY,{"disambiguationData":[OSD([sQuery(id+"F15.wireOp",EDGE,"E70"),sQuery(id+"F15.wireOp",EDGE,"E71"),sQuery(id+"F15.wireOp",EDGE,"E73.MirrorCS"),sQuery(id+"F15.wireOp",EDGE,"E74.MirrorCS")])]});
            var Q60;
            Q60=makeQuery(id+"FeenwNvDrwZ4BJb_3.60.F16.opExtrude","SWEPT_BODY",BODY,{"disambiguationData":[OSD([sQuery(id+"F15.wireOp",EDGE,"E70"),sQuery(id+"F15.wireOp",EDGE,"E71"),sQuery(id+"F15.wireOp",EDGE,"E73.MirrorCS"),sQuery(id+"F15.wireOp",EDGE,"E74.MirrorCS")])]});
            var Q61;
            Q61=makeQuery(id+"FeenwNvDrwZ4BJb_3.61.F16.opExtrude","SWEPT_BODY",BODY,{"disambiguationData":[OSD([sQuery(id+"F15.wireOp",EDGE,"E70"),sQuery(id+"F15.wireOp",EDGE,"E71"),sQuery(id+"F15.wireOp",EDGE,"E73.MirrorCS"),sQuery(id+"F15.wireOp",EDGE,"E74.MirrorCS")])]});
            var Q62;
            Q62=makeQuery(id+"FeenwNvDrwZ4BJb_3.62.F16.opExtrude","SWEPT_BODY",BODY,{"disambiguationData":[OSD([sQuery(id+"F15.wireOp",EDGE,"E70"),sQuery(id+"F15.wireOp",EDGE,"E71"),sQuery(id+"F15.wireOp",EDGE,"E73.MirrorCS"),sQuery(id+"F15.wireOp",EDGE,"E74.MirrorCS")])]});
            var Q63;
            Q63=makeQuery(id+"FeenwNvDrwZ4BJb_3.63.F16.opExtrude","SWEPT_BODY",BODY,{"disambiguationData":[OSD([sQuery(id+"F15.wireOp",EDGE,"E70"),sQuery(id+"F15.wireOp",EDGE,"E71"),sQuery(id+"F15.wireOp",EDGE,"E73.MirrorCS"),sQuery(id+"F15.wireOp",EDGE,"E74.MirrorCS")])]});
            var Q64;
            Q64=makeQuery(id+"FeenwNvDrwZ4BJb_3.64.F16.opExtrude","SWEPT_BODY",BODY,{"disambiguationData":[OSD([sQuery(id+"F15.wireOp",EDGE,"E70"),sQuery(id+"F15.wireOp",EDGE,"E71"),sQuery(id+"F15.wireOp",EDGE,"E73.MirrorCS"),sQuery(id+"F15.wireOp",EDGE,"E74.MirrorCS")])]});
            var Q65;
            Q65=makeQuery(id+"FeenwNvDrwZ4BJb_3.65.F16.opExtrude","SWEPT_BODY",BODY,{"disambiguationData":[OSD([sQuery(id+"F15.wireOp",EDGE,"E70"),sQuery(id+"F15.wireOp",EDGE,"E71"),sQuery(id+"F15.wireOp",EDGE,"E73.MirrorCS"),sQuery(id+"F15.wireOp",EDGE,"E74.MirrorCS")])]});
            var Q66;
            Q66=makeQuery(id+"FeenwNvDrwZ4BJb_3.66.F16.opExtrude","SWEPT_BODY",BODY,{"disambiguationData":[OSD([sQuery(id+"F15.wireOp",EDGE,"E70"),sQuery(id+"F15.wireOp",EDGE,"E71"),sQuery(id+"F15.wireOp",EDGE,"E73.MirrorCS"),sQuery(id+"F15.wireOp",EDGE,"E74.MirrorCS")])]});
            var Q67;
            Q67=makeQuery(id+"FeenwNvDrwZ4BJb_3.67.F16.opExtrude","SWEPT_BODY",BODY,{"disambiguationData":[OSD([sQuery(id+"F15.wireOp",EDGE,"E70"),sQuery(id+"F15.wireOp",EDGE,"E71"),sQuery(id+"F15.wireOp",EDGE,"E73.MirrorCS"),sQuery(id+"F15.wireOp",EDGE,"E74.MirrorCS")])]});
            var Q68;
            Q68=makeQuery(id+"FeenwNvDrwZ4BJb_3.68.F16.opExtrude","SWEPT_BODY",BODY,{"disambiguationData":[OSD([sQuery(id+"F15.wireOp",EDGE,"E70"),sQuery(id+"F15.wireOp",EDGE,"E71"),sQuery(id+"F15.wireOp",EDGE,"E73.MirrorCS"),sQuery(id+"F15.wireOp",EDGE,"E74.MirrorCS")])]});
            var Q69;
            Q69=makeQuery(id+"FeenwNvDrwZ4BJb_3.69.F16.opExtrude","SWEPT_BODY",BODY,{"disambiguationData":[OSD([sQuery(id+"F15.wireOp",EDGE,"E70"),sQuery(id+"F15.wireOp",EDGE,"E71"),sQuery(id+"F15.wireOp",EDGE,"E73.MirrorCS"),sQuery(id+"F15.wireOp",EDGE,"E74.MirrorCS")])]});
            var Q70;
            Q70=makeQuery(id+"FeenwNvDrwZ4BJb_3.70.F16.opExtrude","SWEPT_BODY",BODY,{"disambiguationData":[OSD([sQuery(id+"F15.wireOp",EDGE,"E70"),sQuery(id+"F15.wireOp",EDGE,"E71"),sQuery(id+"F15.wireOp",EDGE,"E73.MirrorCS"),sQuery(id+"F15.wireOp",EDGE,"E74.MirrorCS")])]});
            var Q71;
            Q71=makeQuery(id+"FeenwNvDrwZ4BJb_3.71.F16.opExtrude","SWEPT_BODY",BODY,{"disambiguationData":[OSD([sQuery(id+"F15.wireOp",EDGE,"E70"),sQuery(id+"F15.wireOp",EDGE,"E71"),sQuery(id+"F15.wireOp",EDGE,"E73.MirrorCS"),sQuery(id+"F15.wireOp",EDGE,"E74.MirrorCS")])]});
            var Q72;
            Q72=makeQuery(id+"FeenwNvDrwZ4BJb_3.72.F16.opExtrude","SWEPT_BODY",BODY,{"disambiguationData":[OSD([sQuery(id+"F15.wireOp",EDGE,"E70"),sQuery(id+"F15.wireOp",EDGE,"E71"),sQuery(id+"F15.wireOp",EDGE,"E73.MirrorCS"),sQuery(id+"F15.wireOp",EDGE,"E74.MirrorCS")])]});
            var Q73;
            Q73=makeQuery(id+"FeenwNvDrwZ4BJb_3.73.F16.opExtrude","SWEPT_BODY",BODY,{"disambiguationData":[OSD([sQuery(id+"F15.wireOp",EDGE,"E70"),sQuery(id+"F15.wireOp",EDGE,"E71"),sQuery(id+"F15.wireOp",EDGE,"E73.MirrorCS"),sQuery(id+"F15.wireOp",EDGE,"E74.MirrorCS")])]});
            var Q74;
            Q74=makeQuery(id+"FeenwNvDrwZ4BJb_3.74.F16.opExtrude","SWEPT_BODY",BODY,{"disambiguationData":[OSD([sQuery(id+"F15.wireOp",EDGE,"E70"),sQuery(id+"F15.wireOp",EDGE,"E71"),sQuery(id+"F15.wireOp",EDGE,"E73.MirrorCS"),sQuery(id+"F15.wireOp",EDGE,"E74.MirrorCS")])]});
            var Q75;
            Q75=makeQuery(id+"FeenwNvDrwZ4BJb_3.75.F16.opExtrude","SWEPT_BODY",BODY,{"disambiguationData":[OSD([sQuery(id+"F15.wireOp",EDGE,"E70"),sQuery(id+"F15.wireOp",EDGE,"E71"),sQuery(id+"F15.wireOp",EDGE,"E73.MirrorCS"),sQuery(id+"F15.wireOp",EDGE,"E74.MirrorCS")])]});
            var Q76;
            Q76=makeQuery(id+"FeenwNvDrwZ4BJb_3.76.F16.opExtrude","SWEPT_BODY",BODY,{"disambiguationData":[OSD([sQuery(id+"F15.wireOp",EDGE,"E70"),sQuery(id+"F15.wireOp",EDGE,"E71"),sQuery(id+"F15.wireOp",EDGE,"E73.MirrorCS"),sQuery(id+"F15.wireOp",EDGE,"E74.MirrorCS")])]});
            var Q77;
            Q77=makeQuery(id+"FeenwNvDrwZ4BJb_3.77.F16.opExtrude","SWEPT_BODY",BODY,{"disambiguationData":[OSD([sQuery(id+"F15.wireOp",EDGE,"E70"),sQuery(id+"F15.wireOp",EDGE,"E71"),sQuery(id+"F15.wireOp",EDGE,"E73.MirrorCS"),sQuery(id+"F15.wireOp",EDGE,"E74.MirrorCS")])]});
            var Q78;
            Q78=makeQuery(id+"FeenwNvDrwZ4BJb_3.78.F16.opExtrude","SWEPT_BODY",BODY,{"disambiguationData":[OSD([sQuery(id+"F15.wireOp",EDGE,"E70"),sQuery(id+"F15.wireOp",EDGE,"E71"),sQuery(id+"F15.wireOp",EDGE,"E73.MirrorCS"),sQuery(id+"F15.wireOp",EDGE,"E74.MirrorCS")])]});
            var Q79;
            Q79=makeQuery(id+"FeenwNvDrwZ4BJb_3.79.F16.opExtrude","SWEPT_BODY",BODY,{"disambiguationData":[OSD([sQuery(id+"F15.wireOp",EDGE,"E70"),sQuery(id+"F15.wireOp",EDGE,"E71"),sQuery(id+"F15.wireOp",EDGE,"E73.MirrorCS"),sQuery(id+"F15.wireOp",EDGE,"E74.MirrorCS")])]});
            var Q80;
            Q80=makeQuery(id+"FeenwNvDrwZ4BJb_3.80.F16.opExtrude","SWEPT_BODY",BODY,{"disambiguationData":[OSD([sQuery(id+"F15.wireOp",EDGE,"E70"),sQuery(id+"F15.wireOp",EDGE,"E71"),sQuery(id+"F15.wireOp",EDGE,"E73.MirrorCS"),sQuery(id+"F15.wireOp",EDGE,"E74.MirrorCS")])]});
            var Q81;
            Q81=makeQuery(id+"FeenwNvDrwZ4BJb_3.81.F16.opExtrude","SWEPT_BODY",BODY,{"disambiguationData":[OSD([sQuery(id+"F15.wireOp",EDGE,"E70"),sQuery(id+"F15.wireOp",EDGE,"E71"),sQuery(id+"F15.wireOp",EDGE,"E73.MirrorCS"),sQuery(id+"F15.wireOp",EDGE,"E74.MirrorCS")])]});
            var Q82;
            Q82=makeQuery(id+"FeenwNvDrwZ4BJb_3.82.F16.opExtrude","SWEPT_BODY",BODY,{"disambiguationData":[OSD([sQuery(id+"F15.wireOp",EDGE,"E70"),sQuery(id+"F15.wireOp",EDGE,"E71"),sQuery(id+"F15.wireOp",EDGE,"E73.MirrorCS"),sQuery(id+"F15.wireOp",EDGE,"E74.MirrorCS")])]});
            var Q83;
            Q83=makeQuery(id+"FeenwNvDrwZ4BJb_3.83.F16.opExtrude","SWEPT_BODY",BODY,{"disambiguationData":[OSD([sQuery(id+"F15.wireOp",EDGE,"E70"),sQuery(id+"F15.wireOp",EDGE,"E71"),sQuery(id+"F15.wireOp",EDGE,"E73.MirrorCS"),sQuery(id+"F15.wireOp",EDGE,"E74.MirrorCS")])]});
            var Q84;
            Q84=makeQuery(id+"FeenwNvDrwZ4BJb_3.84.F16.opExtrude","SWEPT_BODY",BODY,{"disambiguationData":[OSD([sQuery(id+"F15.wireOp",EDGE,"E70"),sQuery(id+"F15.wireOp",EDGE,"E71"),sQuery(id+"F15.wireOp",EDGE,"E73.MirrorCS"),sQuery(id+"F15.wireOp",EDGE,"E74.MirrorCS")])]});
            var Q85;
            Q85=makeQuery(id+"FeenwNvDrwZ4BJb_3.85.F16.opExtrude","SWEPT_BODY",BODY,{"disambiguationData":[OSD([sQuery(id+"F15.wireOp",EDGE,"E70"),sQuery(id+"F15.wireOp",EDGE,"E71"),sQuery(id+"F15.wireOp",EDGE,"E73.MirrorCS"),sQuery(id+"F15.wireOp",EDGE,"E74.MirrorCS")])]});
            var Q86;
            Q86=makeQuery(id+"FeenwNvDrwZ4BJb_3.86.F16.opExtrude","SWEPT_BODY",BODY,{"disambiguationData":[OSD([sQuery(id+"F15.wireOp",EDGE,"E70"),sQuery(id+"F15.wireOp",EDGE,"E71"),sQuery(id+"F15.wireOp",EDGE,"E73.MirrorCS"),sQuery(id+"F15.wireOp",EDGE,"E74.MirrorCS")])]});
            var Q87;
            Q87=makeQuery(id+"FeenwNvDrwZ4BJb_3.87.F16.opExtrude","SWEPT_BODY",BODY,{"disambiguationData":[OSD([sQuery(id+"F15.wireOp",EDGE,"E70"),sQuery(id+"F15.wireOp",EDGE,"E71"),sQuery(id+"F15.wireOp",EDGE,"E73.MirrorCS"),sQuery(id+"F15.wireOp",EDGE,"E74.MirrorCS")])]});
            var Q88;
            Q88=makeQuery(id+"FeenwNvDrwZ4BJb_3.88.F16.opExtrude","SWEPT_BODY",BODY,{"disambiguationData":[OSD([sQuery(id+"F15.wireOp",EDGE,"E70"),sQuery(id+"F15.wireOp",EDGE,"E71"),sQuery(id+"F15.wireOp",EDGE,"E73.MirrorCS"),sQuery(id+"F15.wireOp",EDGE,"E74.MirrorCS")])]});
            var Q89;
            Q89=makeQuery(id+"FeenwNvDrwZ4BJb_3.89.F16.opExtrude","SWEPT_BODY",BODY,{"disambiguationData":[OSD([sQuery(id+"F15.wireOp",EDGE,"E70"),sQuery(id+"F15.wireOp",EDGE,"E71"),sQuery(id+"F15.wireOp",EDGE,"E73.MirrorCS"),sQuery(id+"F15.wireOp",EDGE,"E74.MirrorCS")])]});
            var Q90;
            Q90=makeQuery(id+"FeenwNvDrwZ4BJb_3.90.F16.opExtrude","SWEPT_BODY",BODY,{"disambiguationData":[OSD([sQuery(id+"F15.wireOp",EDGE,"E70"),sQuery(id+"F15.wireOp",EDGE,"E71"),sQuery(id+"F15.wireOp",EDGE,"E73.MirrorCS"),sQuery(id+"F15.wireOp",EDGE,"E74.MirrorCS")])]});
            var Q91;
            Q91=makeQuery(id+"FeenwNvDrwZ4BJb_3.91.F16.opExtrude","SWEPT_BODY",BODY,{"disambiguationData":[OSD([sQuery(id+"F15.wireOp",EDGE,"E70"),sQuery(id+"F15.wireOp",EDGE,"E71"),sQuery(id+"F15.wireOp",EDGE,"E73.MirrorCS"),sQuery(id+"F15.wireOp",EDGE,"E74.MirrorCS")])]});
            var Q92;
            Q92=makeQuery(id+"FeenwNvDrwZ4BJb_3.92.F16.opExtrude","SWEPT_BODY",BODY,{"disambiguationData":[OSD([sQuery(id+"F15.wireOp",EDGE,"E70"),sQuery(id+"F15.wireOp",EDGE,"E71"),sQuery(id+"F15.wireOp",EDGE,"E73.MirrorCS"),sQuery(id+"F15.wireOp",EDGE,"E74.MirrorCS")])]});
            var Q93;
            Q93=makeQuery(id+"FeenwNvDrwZ4BJb_3.93.F16.opExtrude","SWEPT_BODY",BODY,{"disambiguationData":[OSD([sQuery(id+"F15.wireOp",EDGE,"E70"),sQuery(id+"F15.wireOp",EDGE,"E71"),sQuery(id+"F15.wireOp",EDGE,"E73.MirrorCS"),sQuery(id+"F15.wireOp",EDGE,"E74.MirrorCS")])]});
            var Q94;
            Q94=makeQuery(id+"FeenwNvDrwZ4BJb_3.94.F16.opExtrude","SWEPT_BODY",BODY,{"disambiguationData":[OSD([sQuery(id+"F15.wireOp",EDGE,"E70"),sQuery(id+"F15.wireOp",EDGE,"E71"),sQuery(id+"F15.wireOp",EDGE,"E73.MirrorCS"),sQuery(id+"F15.wireOp",EDGE,"E74.MirrorCS")])]});
            var Q95;
            Q95=makeQuery(id+"FeenwNvDrwZ4BJb_3.95.F16.opExtrude","SWEPT_BODY",BODY,{"disambiguationData":[OSD([sQuery(id+"F15.wireOp",EDGE,"E70"),sQuery(id+"F15.wireOp",EDGE,"E71"),sQuery(id+"F15.wireOp",EDGE,"E73.MirrorCS"),sQuery(id+"F15.wireOp",EDGE,"E74.MirrorCS")])]});
            var Q96;
            Q96=makeQuery(id+"FeenwNvDrwZ4BJb_3.96.F16.opExtrude","SWEPT_BODY",BODY,{"disambiguationData":[OSD([sQuery(id+"F15.wireOp",EDGE,"E70"),sQuery(id+"F15.wireOp",EDGE,"E71"),sQuery(id+"F15.wireOp",EDGE,"E73.MirrorCS"),sQuery(id+"F15.wireOp",EDGE,"E74.MirrorCS")])]});
            var Q97;
            Q97=makeQuery(id+"FeenwNvDrwZ4BJb_3.97.F16.opExtrude","SWEPT_BODY",BODY,{"disambiguationData":[OSD([sQuery(id+"F15.wireOp",EDGE,"E70"),sQuery(id+"F15.wireOp",EDGE,"E71"),sQuery(id+"F15.wireOp",EDGE,"E73.MirrorCS"),sQuery(id+"F15.wireOp",EDGE,"E74.MirrorCS")])]});
            var Q98;
            Q98=makeQuery(id+"FeenwNvDrwZ4BJb_3.98.F16.opExtrude","SWEPT_BODY",BODY,{"disambiguationData":[OSD([sQuery(id+"F15.wireOp",EDGE,"E70"),sQuery(id+"F15.wireOp",EDGE,"E71"),sQuery(id+"F15.wireOp",EDGE,"E73.MirrorCS"),sQuery(id+"F15.wireOp",EDGE,"E74.MirrorCS")])]});
            var Q99;
            Q99=makeQuery(id+"FeenwNvDrwZ4BJb_3.99.F16.opExtrude","SWEPT_BODY",BODY,{"disambiguationData":[OSD([sQuery(id+"F15.wireOp",EDGE,"E70"),sQuery(id+"F15.wireOp",EDGE,"E71"),sQuery(id+"F15.wireOp",EDGE,"E73.MirrorCS"),sQuery(id+"F15.wireOp",EDGE,"E74.MirrorCS")])]});
            var Q100;
            Q100=makeQuery(id+"FeenwNvDrwZ4BJb_3.100.F16.opExtrude","SWEPT_BODY",BODY,{"disambiguationData":[OSD([sQuery(id+"F15.wireOp",EDGE,"E70"),sQuery(id+"F15.wireOp",EDGE,"E71"),sQuery(id+"F15.wireOp",EDGE,"E73.MirrorCS"),sQuery(id+"F15.wireOp",EDGE,"E74.MirrorCS")])]});
            var Q101;
            Q101=makeQuery(id+"FeenwNvDrwZ4BJb_3.101.F16.opExtrude","SWEPT_BODY",BODY,{"disambiguationData":[OSD([sQuery(id+"F15.wireOp",EDGE,"E70"),sQuery(id+"F15.wireOp",EDGE,"E71"),sQuery(id+"F15.wireOp",EDGE,"E73.MirrorCS"),sQuery(id+"F15.wireOp",EDGE,"E74.MirrorCS")])]});
            var Q102;
            Q102=makeQuery(id+"FeenwNvDrwZ4BJb_3.102.F16.opExtrude","SWEPT_BODY",BODY,{"disambiguationData":[OSD([sQuery(id+"F15.wireOp",EDGE,"E70"),sQuery(id+"F15.wireOp",EDGE,"E71"),sQuery(id+"F15.wireOp",EDGE,"E73.MirrorCS"),sQuery(id+"F15.wireOp",EDGE,"E74.MirrorCS")])]});
            var Q103;
            Q103=makeQuery(id+"FeenwNvDrwZ4BJb_3.103.F16.opExtrude","SWEPT_BODY",BODY,{"disambiguationData":[OSD([sQuery(id+"F15.wireOp",EDGE,"E70"),sQuery(id+"F15.wireOp",EDGE,"E71"),sQuery(id+"F15.wireOp",EDGE,"E73.MirrorCS"),sQuery(id+"F15.wireOp",EDGE,"E74.MirrorCS")])]});
            var Q104;
            Q104=makeQuery(id+"FeenwNvDrwZ4BJb_3.104.F16.opExtrude","SWEPT_BODY",BODY,{"disambiguationData":[OSD([sQuery(id+"F15.wireOp",EDGE,"E70"),sQuery(id+"F15.wireOp",EDGE,"E71"),sQuery(id+"F15.wireOp",EDGE,"E73.MirrorCS"),sQuery(id+"F15.wireOp",EDGE,"E74.MirrorCS")])]});
            var Q105;
            Q105=makeQuery(id+"FeenwNvDrwZ4BJb_3.105.F16.opExtrude","SWEPT_BODY",BODY,{"disambiguationData":[OSD([sQuery(id+"F15.wireOp",EDGE,"E70"),sQuery(id+"F15.wireOp",EDGE,"E71"),sQuery(id+"F15.wireOp",EDGE,"E73.MirrorCS"),sQuery(id+"F15.wireOp",EDGE,"E74.MirrorCS")])]});
            var Q106;
            Q106=makeQuery(id+"FeenwNvDrwZ4BJb_3.106.F16.opExtrude","SWEPT_BODY",BODY,{"disambiguationData":[OSD([sQuery(id+"F15.wireOp",EDGE,"E70"),sQuery(id+"F15.wireOp",EDGE,"E71"),sQuery(id+"F15.wireOp",EDGE,"E73.MirrorCS"),sQuery(id+"F15.wireOp",EDGE,"E74.MirrorCS")])]});
            var Q107;
            Q107=makeQuery(id+"FeenwNvDrwZ4BJb_3.107.F16.opExtrude","SWEPT_BODY",BODY,{"disambiguationData":[OSD([sQuery(id+"F15.wireOp",EDGE,"E70"),sQuery(id+"F15.wireOp",EDGE,"E71"),sQuery(id+"F15.wireOp",EDGE,"E73.MirrorCS"),sQuery(id+"F15.wireOp",EDGE,"E74.MirrorCS")])]});
            var Q108;
            Q108=makeQuery(id+"FeenwNvDrwZ4BJb_3.108.F16.opExtrude","SWEPT_BODY",BODY,{"disambiguationData":[OSD([sQuery(id+"F15.wireOp",EDGE,"E70"),sQuery(id+"F15.wireOp",EDGE,"E71"),sQuery(id+"F15.wireOp",EDGE,"E73.MirrorCS"),sQuery(id+"F15.wireOp",EDGE,"E74.MirrorCS")])]});
            var Q109;
            Q109=makeQuery(id+"FeenwNvDrwZ4BJb_3.109.F16.opExtrude","SWEPT_BODY",BODY,{"disambiguationData":[OSD([sQuery(id+"F15.wireOp",EDGE,"E70"),sQuery(id+"F15.wireOp",EDGE,"E71"),sQuery(id+"F15.wireOp",EDGE,"E73.MirrorCS"),sQuery(id+"F15.wireOp",EDGE,"E74.MirrorCS")])]});
            var Q110;
            Q110=makeQuery(id+"FeenwNvDrwZ4BJb_3.110.F16.opExtrude","SWEPT_BODY",BODY,{"disambiguationData":[OSD([sQuery(id+"F15.wireOp",EDGE,"E70"),sQuery(id+"F15.wireOp",EDGE,"E71"),sQuery(id+"F15.wireOp",EDGE,"E73.MirrorCS"),sQuery(id+"F15.wireOp",EDGE,"E74.MirrorCS")])]});
            var Q111;
            Q111=makeQuery(id+"FeenwNvDrwZ4BJb_3.111.F16.opExtrude","SWEPT_BODY",BODY,{"disambiguationData":[OSD([sQuery(id+"F15.wireOp",EDGE,"E70"),sQuery(id+"F15.wireOp",EDGE,"E71"),sQuery(id+"F15.wireOp",EDGE,"E73.MirrorCS"),sQuery(id+"F15.wireOp",EDGE,"E74.MirrorCS")])]});
            var Q112;
            Q112=makeQuery(id+"FeenwNvDrwZ4BJb_3.112.F16.opExtrude","SWEPT_BODY",BODY,{"disambiguationData":[OSD([sQuery(id+"F15.wireOp",EDGE,"E70"),sQuery(id+"F15.wireOp",EDGE,"E71"),sQuery(id+"F15.wireOp",EDGE,"E73.MirrorCS"),sQuery(id+"F15.wireOp",EDGE,"E74.MirrorCS")])]});
            var Q113;
            Q113=makeQuery(id+"FeenwNvDrwZ4BJb_3.113.F16.opExtrude","SWEPT_BODY",BODY,{"disambiguationData":[OSD([sQuery(id+"F15.wireOp",EDGE,"E70"),sQuery(id+"F15.wireOp",EDGE,"E71"),sQuery(id+"F15.wireOp",EDGE,"E73.MirrorCS"),sQuery(id+"F15.wireOp",EDGE,"E74.MirrorCS")])]});
            var Q114;
            Q114=makeQuery(id+"FeenwNvDrwZ4BJb_3.114.F16.opExtrude","SWEPT_BODY",BODY,{"disambiguationData":[OSD([sQuery(id+"F15.wireOp",EDGE,"E70"),sQuery(id+"F15.wireOp",EDGE,"E71"),sQuery(id+"F15.wireOp",EDGE,"E73.MirrorCS"),sQuery(id+"F15.wireOp",EDGE,"E74.MirrorCS")])]});
            var Q115;
            Q115=makeQuery(id+"FeenwNvDrwZ4BJb_3.115.F16.opExtrude","SWEPT_BODY",BODY,{"disambiguationData":[OSD([sQuery(id+"F15.wireOp",EDGE,"E70"),sQuery(id+"F15.wireOp",EDGE,"E71"),sQuery(id+"F15.wireOp",EDGE,"E73.MirrorCS"),sQuery(id+"F15.wireOp",EDGE,"E74.MirrorCS")])]});
            var Q116;
            Q116=makeQuery(id+"FeenwNvDrwZ4BJb_3.116.F16.opExtrude","SWEPT_BODY",BODY,{"disambiguationData":[OSD([sQuery(id+"F15.wireOp",EDGE,"E70"),sQuery(id+"F15.wireOp",EDGE,"E71"),sQuery(id+"F15.wireOp",EDGE,"E73.MirrorCS"),sQuery(id+"F15.wireOp",EDGE,"E74.MirrorCS")])]});
            var Q117;
            Q117=makeQuery(id+"FeenwNvDrwZ4BJb_3.117.F16.opExtrude","SWEPT_BODY",BODY,{"disambiguationData":[OSD([sQuery(id+"F15.wireOp",EDGE,"E70"),sQuery(id+"F15.wireOp",EDGE,"E71"),sQuery(id+"F15.wireOp",EDGE,"E73.MirrorCS"),sQuery(id+"F15.wireOp",EDGE,"E74.MirrorCS")])]});
            var Q118;
            Q118=makeQuery(id+"FeenwNvDrwZ4BJb_3.118.F16.opExtrude","SWEPT_BODY",BODY,{"disambiguationData":[OSD([sQuery(id+"F15.wireOp",EDGE,"E70"),sQuery(id+"F15.wireOp",EDGE,"E71"),sQuery(id+"F15.wireOp",EDGE,"E73.MirrorCS"),sQuery(id+"F15.wireOp",EDGE,"E74.MirrorCS")])]});
            var Q119;
            Q119=makeQuery(id+"FeenwNvDrwZ4BJb_3.119.F16.opExtrude","SWEPT_BODY",BODY,{"disambiguationData":[OSD([sQuery(id+"F15.wireOp",EDGE,"E70"),sQuery(id+"F15.wireOp",EDGE,"E71"),sQuery(id+"F15.wireOp",EDGE,"E73.MirrorCS"),sQuery(id+"F15.wireOp",EDGE,"E74.MirrorCS")])]});
            var Q120;
            Q120=makeQuery(id+"FeenwNvDrwZ4BJb_3.120.F16.opExtrude","SWEPT_BODY",BODY,{"disambiguationData":[OSD([sQuery(id+"F15.wireOp",EDGE,"E70"),sQuery(id+"F15.wireOp",EDGE,"E71"),sQuery(id+"F15.wireOp",EDGE,"E73.MirrorCS"),sQuery(id+"F15.wireOp",EDGE,"E74.MirrorCS")])]});
            var Q121;
            Q121=makeQuery(id+"FeenwNvDrwZ4BJb_3.121.F16.opExtrude","SWEPT_BODY",BODY,{"disambiguationData":[OSD([sQuery(id+"F15.wireOp",EDGE,"E70"),sQuery(id+"F15.wireOp",EDGE,"E71"),sQuery(id+"F15.wireOp",EDGE,"E73.MirrorCS"),sQuery(id+"F15.wireOp",EDGE,"E74.MirrorCS")])]});
            var Q122;
            Q122=makeQuery(id+"FeenwNvDrwZ4BJb_3.122.F16.opExtrude","SWEPT_BODY",BODY,{"disambiguationData":[OSD([sQuery(id+"F15.wireOp",EDGE,"E70"),sQuery(id+"F15.wireOp",EDGE,"E71"),sQuery(id+"F15.wireOp",EDGE,"E73.MirrorCS"),sQuery(id+"F15.wireOp",EDGE,"E74.MirrorCS")])]});
            var Q123;
            Q123=makeQuery(id+"FeenwNvDrwZ4BJb_3.123.F16.opExtrude","SWEPT_BODY",BODY,{"disambiguationData":[OSD([sQuery(id+"F15.wireOp",EDGE,"E70"),sQuery(id+"F15.wireOp",EDGE,"E71"),sQuery(id+"F15.wireOp",EDGE,"E73.MirrorCS"),sQuery(id+"F15.wireOp",EDGE,"E74.MirrorCS")])]});
            var Q124;
            Q124=makeQuery(id+"FeenwNvDrwZ4BJb_3.124.F16.opExtrude","SWEPT_BODY",BODY,{"disambiguationData":[OSD([sQuery(id+"F15.wireOp",EDGE,"E70"),sQuery(id+"F15.wireOp",EDGE,"E71"),sQuery(id+"F15.wireOp",EDGE,"E73.MirrorCS"),sQuery(id+"F15.wireOp",EDGE,"E74.MirrorCS")])]});
            var Q125;
            Q125=makeQuery(id+"FeenwNvDrwZ4BJb_3.125.F16.opExtrude","SWEPT_BODY",BODY,{"disambiguationData":[OSD([sQuery(id+"F15.wireOp",EDGE,"E70"),sQuery(id+"F15.wireOp",EDGE,"E71"),sQuery(id+"F15.wireOp",EDGE,"E73.MirrorCS"),sQuery(id+"F15.wireOp",EDGE,"E74.MirrorCS")])]});
            var Q126;
            Q126=makeQuery(id+"FeenwNvDrwZ4BJb_3.126.F16.opExtrude","SWEPT_BODY",BODY,{"disambiguationData":[OSD([sQuery(id+"F15.wireOp",EDGE,"E70"),sQuery(id+"F15.wireOp",EDGE,"E71"),sQuery(id+"F15.wireOp",EDGE,"E73.MirrorCS"),sQuery(id+"F15.wireOp",EDGE,"E74.MirrorCS")])]});
            var Q127;
            Q127=makeQuery(id+"FeenwNvDrwZ4BJb_3.127.F16.opExtrude","SWEPT_BODY",BODY,{"disambiguationData":[OSD([sQuery(id+"F15.wireOp",EDGE,"E70"),sQuery(id+"F15.wireOp",EDGE,"E71"),sQuery(id+"F15.wireOp",EDGE,"E73.MirrorCS"),sQuery(id+"F15.wireOp",EDGE,"E74.MirrorCS")])]});
            var Q128;
            Q128=makeQuery(id+"FeenwNvDrwZ4BJb_3.128.F16.opExtrude","SWEPT_BODY",BODY,{"disambiguationData":[OSD([sQuery(id+"F15.wireOp",EDGE,"E70"),sQuery(id+"F15.wireOp",EDGE,"E71"),sQuery(id+"F15.wireOp",EDGE,"E73.MirrorCS"),sQuery(id+"F15.wireOp",EDGE,"E74.MirrorCS")])]});
            var Q129;
            Q129=makeQuery(id+"FeenwNvDrwZ4BJb_3.129.F16.opExtrude","SWEPT_BODY",BODY,{"disambiguationData":[OSD([sQuery(id+"F15.wireOp",EDGE,"E70"),sQuery(id+"F15.wireOp",EDGE,"E71"),sQuery(id+"F15.wireOp",EDGE,"E73.MirrorCS"),sQuery(id+"F15.wireOp",EDGE,"E74.MirrorCS")])]});
            var Q130;
            Q130=makeQuery(id+"FeenwNvDrwZ4BJb_3.130.F16.opExtrude","SWEPT_BODY",BODY,{"disambiguationData":[OSD([sQuery(id+"F15.wireOp",EDGE,"E70"),sQuery(id+"F15.wireOp",EDGE,"E71"),sQuery(id+"F15.wireOp",EDGE,"E73.MirrorCS"),sQuery(id+"F15.wireOp",EDGE,"E74.MirrorCS")])]});
            var Q131;
            Q131=makeQuery(id+"FeenwNvDrwZ4BJb_3.131.F16.opExtrude","SWEPT_BODY",BODY,{"disambiguationData":[OSD([sQuery(id+"F15.wireOp",EDGE,"E70"),sQuery(id+"F15.wireOp",EDGE,"E71"),sQuery(id+"F15.wireOp",EDGE,"E73.MirrorCS"),sQuery(id+"F15.wireOp",EDGE,"E74.MirrorCS")])]});
            var Q132;
            Q132=makeQuery(id+"FeenwNvDrwZ4BJb_3.132.F16.opExtrude","SWEPT_BODY",BODY,{"disambiguationData":[OSD([sQuery(id+"F15.wireOp",EDGE,"E70"),sQuery(id+"F15.wireOp",EDGE,"E71"),sQuery(id+"F15.wireOp",EDGE,"E73.MirrorCS"),sQuery(id+"F15.wireOp",EDGE,"E74.MirrorCS")])]});
            var Q133;
            Q133=makeQuery(id+"FeenwNvDrwZ4BJb_3.133.F16.opExtrude","SWEPT_BODY",BODY,{"disambiguationData":[OSD([sQuery(id+"F15.wireOp",EDGE,"E70"),sQuery(id+"F15.wireOp",EDGE,"E71"),sQuery(id+"F15.wireOp",EDGE,"E73.MirrorCS"),sQuery(id+"F15.wireOp",EDGE,"E74.MirrorCS")])]});
            var Q134;
            Q134=makeQuery(id+"FeenwNvDrwZ4BJb_3.134.F16.opExtrude","SWEPT_BODY",BODY,{"disambiguationData":[OSD([sQuery(id+"F15.wireOp",EDGE,"E70"),sQuery(id+"F15.wireOp",EDGE,"E71"),sQuery(id+"F15.wireOp",EDGE,"E73.MirrorCS"),sQuery(id+"F15.wireOp",EDGE,"E74.MirrorCS")])]});
            var Q135;
            Q135=makeQuery(id+"FeenwNvDrwZ4BJb_3.135.F16.opExtrude","SWEPT_BODY",BODY,{"disambiguationData":[OSD([sQuery(id+"F15.wireOp",EDGE,"E70"),sQuery(id+"F15.wireOp",EDGE,"E71"),sQuery(id+"F15.wireOp",EDGE,"E73.MirrorCS"),sQuery(id+"F15.wireOp",EDGE,"E74.MirrorCS")])]});
            var Q136;
            Q136=makeQuery(id+"FeenwNvDrwZ4BJb_3.136.F16.opExtrude","SWEPT_BODY",BODY,{"disambiguationData":[OSD([sQuery(id+"F15.wireOp",EDGE,"E70"),sQuery(id+"F15.wireOp",EDGE,"E71"),sQuery(id+"F15.wireOp",EDGE,"E73.MirrorCS"),sQuery(id+"F15.wireOp",EDGE,"E74.MirrorCS")])]});
            var Q137;
            Q137=makeQuery(id+"FeenwNvDrwZ4BJb_3.137.F16.opExtrude","SWEPT_BODY",BODY,{"disambiguationData":[OSD([sQuery(id+"F15.wireOp",EDGE,"E70"),sQuery(id+"F15.wireOp",EDGE,"E71"),sQuery(id+"F15.wireOp",EDGE,"E73.MirrorCS"),sQuery(id+"F15.wireOp",EDGE,"E74.MirrorCS")])]});
            var Q138;
            Q138=makeQuery(id+"FeenwNvDrwZ4BJb_3.138.F16.opExtrude","SWEPT_BODY",BODY,{"disambiguationData":[OSD([sQuery(id+"F15.wireOp",EDGE,"E70"),sQuery(id+"F15.wireOp",EDGE,"E71"),sQuery(id+"F15.wireOp",EDGE,"E73.MirrorCS"),sQuery(id+"F15.wireOp",EDGE,"E74.MirrorCS")])]});
            var Q139;
            Q139=makeQuery(id+"FeenwNvDrwZ4BJb_3.139.F16.opExtrude","SWEPT_BODY",BODY,{"disambiguationData":[OSD([sQuery(id+"F15.wireOp",EDGE,"E70"),sQuery(id+"F15.wireOp",EDGE,"E71"),sQuery(id+"F15.wireOp",EDGE,"E73.MirrorCS"),sQuery(id+"F15.wireOp",EDGE,"E74.MirrorCS")])]});
            var Q140;
            Q140=makeQuery(id+"F8.opRevolve","SWEPT_BODY",BODY,{"disambiguationData":[OSD([sQuery(id+"F7.wireOp",EDGE,"E34"),sQuery(id+"F7.wireOp",EDGE,"E35"),sQuery(id+"F7.wireOp",EDGE,"J56ha9Rl-Oytq-WNzu-WkIW-moeN9QV1C7si"),sQuery(id+"F7.wireOp",EDGE,"Ar0ScLw1-YCs2-r5Ne-obxw-UKN6tsXmQNs8"),sQuery(id+"F7.wireOp",EDGE,"Pu9IAod2-zVAE-E8hs-bJWV-M0Kr0XDKnnuQ"),sQuery(id+"F7.wireOp",EDGE,"E36")])]});
            booleanBodies(context, id + "F17", {"operationType" : BooleanOperationType.SUBTRACTION, "tools" : qUnion([Q0, Q1, Q2, Q3, Q4, Q5, Q6, Q7, Q8, Q9, Q10, Q11, Q12, Q13, Q14, Q15, Q16, Q17, Q18, Q19, Q20, Q21, Q22, Q23, Q24, Q25, Q26, Q27, Q28, Q29, Q30, Q31, Q32, Q33, Q34, Q35, Q36, Q37, Q38, Q39, Q40, Q41, Q42, Q43, Q44, Q45, Q46, Q47, Q48, Q49, Q50, Q51, Q52, Q53, Q54, Q55, Q56, Q57, Q58, Q59, Q60, Q61, Q62, Q63, Q64, Q65, Q66, Q67, Q68, Q69, Q70, Q71, Q72, Q73, Q74, Q75, Q76, Q77, Q78, Q79, Q80, Q81, Q82, Q83, Q84, Q85, Q86, Q87, Q88, Q89, Q90, Q91, Q92, Q93, Q94, Q95, Q96, Q97, Q98, Q99, Q100, Q101, Q102, Q103, Q104, Q105, Q106, Q107, Q108, Q109, Q110, Q111, Q112, Q113, Q114, Q115, Q116, Q117, Q118, Q119, Q120, Q121, Q122, Q123, Q124, Q125, Q126, Q127, Q128, Q129, Q130, Q131, Q132, Q133, Q134, Q135, Q136, Q137, Q138, Q139]), "targets" : qUnion([Q140])});
        }
        {
            var Q0;
            Q0=qCreatedBy(makeId("Front.planeOp"),FACE);
            var sketch = newSketch(context, id + "F18", { "sketchPlane" : qUnion([Q0])});
            skPoint(sketch, "E75", {"position": v(-29, 0) * mm});
            skPoint(sketch, "E76", {"position": v(14.5, 0) * mm});
            skLineSegment(sketch, "E77", {"start": v(-29, 0) * mm, "end": v(14.5, 0) * mm});
            skPoint(sketch, "E78", {"position": v(-7.25, 0) * mm});
            skLineSegment(sketch, "E79", {"start": v(-7.25, 0) * mm, "end": v(-7.25, -21.14) * mm, "construction": true});
            skLineSegment(sketch, "E80", {"start": v(-7.25, -11.57) * mm, "end": v(-25.93, -11.57) * mm, "construction": true});
            skPoint(sketch, "E80.endSnap0", {"position": v(-7.25, -11.57) * mm});
            skFitSpline(sketch, "E81", {"points": [v(-7.25, -23.14) * mm, v(-12.27, -22.95) * mm, v(-17.16, -22.53) * mm, v(-25.32, -20.9) * mm, v(-27, -19.23) * mm, v(-27.74, -15.85) * mm, v(-27.93, -11.57) * mm], "startDerivative": vector(-33.14, 0.1) * mm, "endDerivative": vector(0, 32.1) * mm});
            skFitSpline(sketch, "E82.MirrorCS", {"points": [v(-7.25, 0) * mm, v(-12.27, -0.2) * mm, v(-17.16, -0.6) * mm, v(-25.32, -2.24) * mm, v(-27, -3.9) * mm, v(-27.74, -7.3) * mm, v(-27.93, -11.57) * mm], "startDerivative": vector(-33.14, -0.1) * mm, "endDerivative": vector(0, -32.1) * mm});
            skFitSpline(sketch, "E83.MirrorCS", {"points": [v(-7.25, 0) * mm, v(-2.23, -0.2) * mm, v(2.66, -0.6) * mm, v(10.82, -2.24) * mm, v(12.5, -3.9) * mm, v(13.24, -7.3) * mm, v(13.43, -11.57) * mm], "startDerivative": vector(33.14, -0.1) * mm, "endDerivative": vector(0, -32.1) * mm});
            skFitSpline(sketch, "E84.MirrorCS", {"points": [v(-7.25, -23.14) * mm, v(-2.23, -22.95) * mm, v(2.66, -22.53) * mm, v(10.82, -20.9) * mm, v(12.5, -19.23) * mm, v(13.24, -15.85) * mm, v(13.43, -11.57) * mm], "startDerivative": vector(33.14, 0.1) * mm, "endDerivative": vector(0, 32.1) * mm});
            skLineSegment(sketch, "E85", {"start": v(-7.25, -21.14) * mm, "end": v(-7.25, -23.14) * mm, "construction": true});
            skFitSpline(sketch, "E86", {"points": [v(-7.25, -21.14) * mm, v(-12.23, -20.95) * mm, v(-16.98, -20.54) * mm, v(-24.5, -19.08) * mm, v(-25.24, -18.26) * mm, v(-25.75, -15.7) * mm, v(-25.93, -11.57) * mm], "startDerivative": vector(-12.93, 0) * mm, "endDerivative": vector(0, 29.91) * mm});
            skLineSegment(sketch, "E87", {"start": v(-25.93, -11.57) * mm, "end": v(-27.93, -11.57) * mm, "construction": true});
            skFitSpline(sketch, "E88.MirrorCS", {"points": [v(-7.25, -2) * mm, v(-12.23, -2.2) * mm, v(-16.98, -2.6) * mm, v(-24.5, -4.06) * mm, v(-25.24, -4.88) * mm, v(-25.75, -7.44) * mm, v(-25.93, -11.57) * mm], "startDerivative": vector(-12.93, 0) * mm, "endDerivative": vector(0, -29.91) * mm});
            skFitSpline(sketch, "E89.MirrorCS", {"points": [v(-7.25, -21.14) * mm, v(-2.27, -20.95) * mm, v(2.48, -20.54) * mm, v(10, -19.08) * mm, v(10.74, -18.26) * mm, v(11.25, -15.7) * mm, v(11.43, -11.57) * mm], "startDerivative": vector(12.93, 0) * mm, "endDerivative": vector(0, 29.91) * mm});
            skFitSpline(sketch, "E90.MirrorCS", {"points": [v(-7.25, -2) * mm, v(-2.27, -2.2) * mm, v(2.48, -2.6) * mm, v(10, -4.06) * mm, v(10.74, -4.88) * mm, v(11.25, -7.44) * mm, v(11.43, -11.57) * mm], "startDerivative": vector(12.93, 0) * mm, "endDerivative": vector(0, -29.91) * mm});
            skLineSegment(sketch, "E91", {"start": v(-7.25, 0) * mm, "end": v(-7.25, 16.78) * mm, "construction": true});
            skLineSegment(sketch, "E92", {"start": v(-27.74, -15.85) * mm, "end": v(-25.75, -15.7) * mm, "construction": true});
            skLineSegment(sketch, "E93", {"start": v(-27, -19.23) * mm, "end": v(-25.24, -18.26) * mm, "construction": true});
            skLineSegment(sketch, "E94", {"start": v(-25.32, -20.9) * mm, "end": v(-24.5, -19.08) * mm, "construction": true});
            skLineSegment(sketch, "E95", {"start": v(-17.16, -22.53) * mm, "end": v(-16.98, -20.54) * mm, "construction": true});
            skLineSegment(sketch, "E96", {"start": v(-12.27, -22.95) * mm, "end": v(-12.23, -20.95) * mm, "construction": true});
            skLineSegment(sketch, "E97", {"start": v(-27.93, -11.57) * mm, "end": v(-28.93, -11.57) * mm, "construction": true});
            skSolve(sketch);
        }
        {
            var Q0;
            Q0=makeQuery(id+"F18.imprint","IMPRINT",FACE,{"disambiguationData":[TD([[makeQuery(id+"F18.imprint","IMPRINT",EDGE,{"derivedFrom":sQuery(id+"F18.wireOp",EDGE,"E81")}),-1.0]])]});
            extrude(context, id + "F19", {"entities" : qUnion([Q0]), "endBound" : BoundingType.SYMMETRIC, "depth" : 1.6 * mm});
        }
    });
